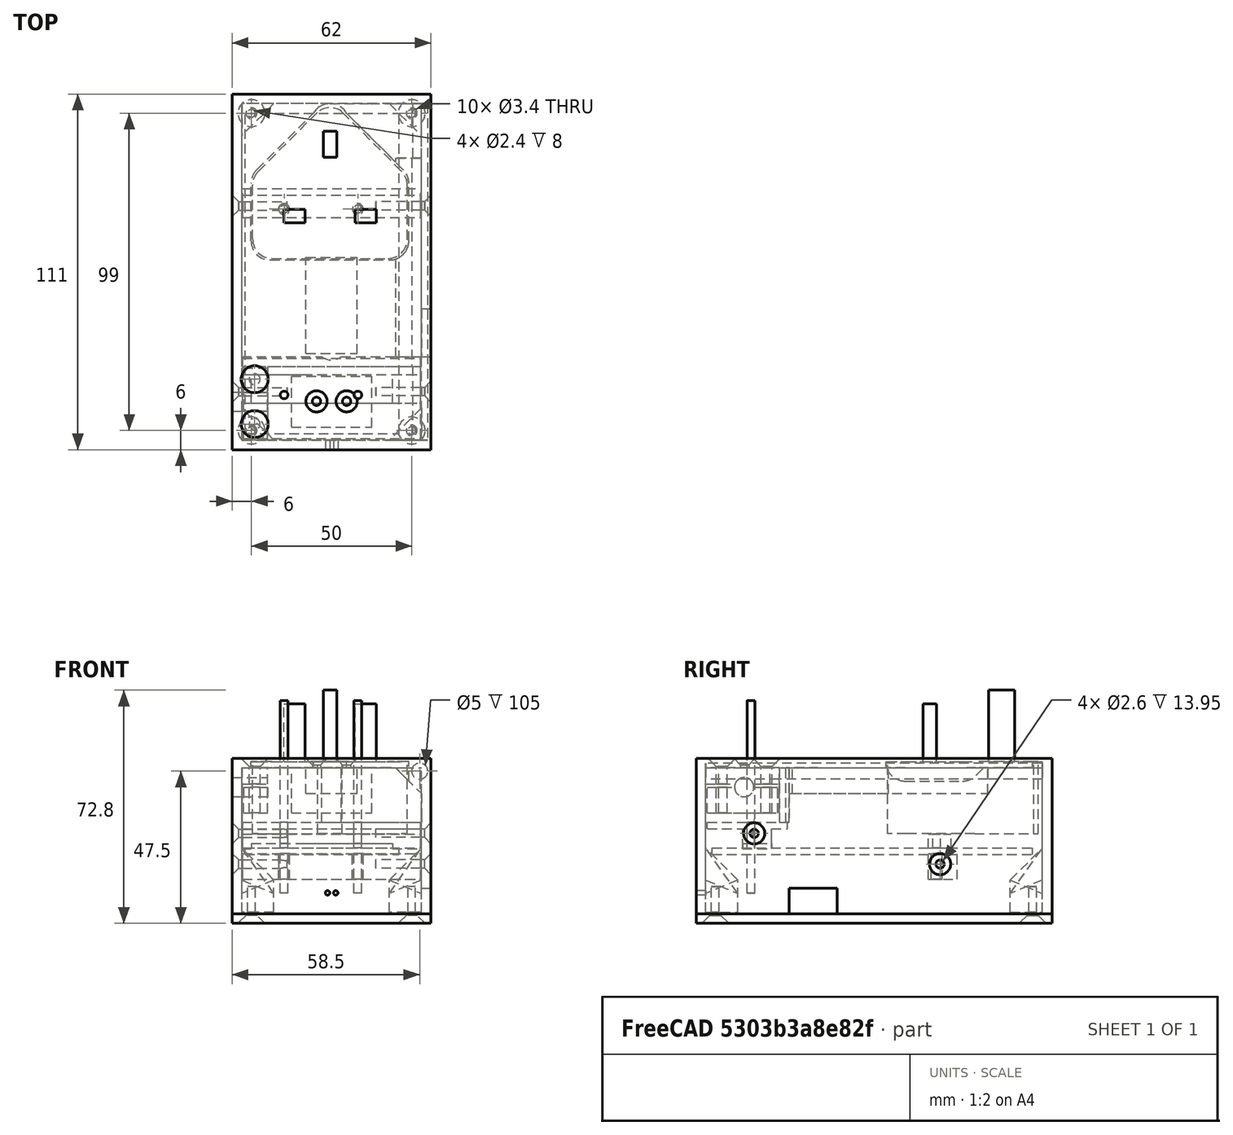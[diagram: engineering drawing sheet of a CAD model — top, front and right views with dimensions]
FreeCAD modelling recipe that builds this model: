
FCSTD DOCUMENT  (FreeCAD 0.16R6703 (Git))
Label: echopi
License: All rights reserved
LicenseURL: http://en.wikipedia.org/wiki/All_rights_reserved
objects: Part::Cut×64, Part::Fuse×35, Part::Box×34, Part::Cylinder×30, Part::Fillet×8, Part::Chamfer×5, Part::Cone×5, Part::Mirroring×5, Part::MultiCommon×2, App::DocumentObjectGroup×1
note: 188 computed .brp shape members not serialized (recipe doc carries the construction recipe); baked Part::Feature solids carry a one-line shape summary decoded from their .brp

FEATURE [Part::Box] Box  label="Cube"
  Height = 18
  Length = 6.6
  Placement = pos=(7.8,-2.2,0) rot=(0,0,1;0rad)
  Width = 4.2
FEATURE [Part::Box] Box001  label="Cube001"
  Height = 18
  Length = 6.6
  Placement = pos=(-14.4,-2.2,0) rot=(0,0,1;0rad)
  Width = 4.2
FEATURE [Part::Box] Box002  label="Cube002"
  Height = 22.3
  Length = 4.2
  Placement = pos=(-2.1,18.2,0) rot=(0,0,1;0rad)
  Width = 8.2
FEATURE [Part::Box] Box003  label="Cube003"
  Height = 50
  Length = 49.2
  Placement = pos=(-24.6,-13.8,-50) rot=(0,0,1;0rad)
  Width = 50.4
FEATURE [Part::Chamfer] Chamfer
  Base = -> Box003
  Edges = 1 edges r=24: [Edge3]
FEATURE [Part::Chamfer] Chamfer001
  Base = -> Chamfer
  Edges = 1 edges r=24: [Edge15]
FEATURE [Part::Fillet] Fillet
  Base = -> Chamfer001
  Edges = 1 edges r=6: [Edge14]
FEATURE [Part::Fillet] Fillet001
  Base = -> Fillet
  Edges = 1 edges r=6: [Edge9]
FEATURE [Part::Fillet] Fillet002
  Base = -> Fillet001
  Edges = 1 edges r=6: [Edge19]
FEATURE [Part::Fillet] Fillet003
  Base = -> Fillet002
  Edges = 1 edges r=6: [Edge17]
FEATURE [Part::Cylinder] Cylinder
  Angle = 360
  Height = 70
  Placement = pos=(0,27.75,-60) rot=(0,0,1;0rad)
  Radius = 6
FEATURE [Part::Box] Box004  label="Cube004"
  Height = 100
  Length = 50
  Placement = pos=(-25,-18,-60) rot=(0,0,1;0rad)
  Width = 50
FEATURE [Part::Fuse] Fusion
  Base = -> Cylinder
  Tool = -> Box004
FEATURE [Part::MultiCommon] Common
  Shapes = -> [Fillet003,Fusion]
FEATURE [Part::Fuse] Fusion001
  Base = -> Box002
  Tool = -> Common
FEATURE [Part::Fuse] Fusion002
  Base = -> Box001
  Tool = -> Fusion001
FEATURE [Part::Fuse] Fusion003  label="plug-blank-a"
  Base = -> Box
  Tool = -> Fusion002
FEATURE [Part::Box] Box005  label="Cube005"
  Height = 48.5
  Length = 62
  Placement = pos=(-31,-73,-48.5) rot=(0,0,1;0rad)
  Width = 111
FEATURE [Part::Box] Box006  label="Cube006"
  Height = 101
  Length = 50
  Placement = pos=(-25,-16,-123.5) rot=(0,0,1;0rad)
  Width = 50
FEATURE [Part::Cut] Cut  label="plug-blank"
  Base = -> Fusion003
  Placement = pos=(-0.5,0,-1) rot=(0,0,1;0rad)
  Tool = -> Box006
FEATURE [Part::Box] Box007  label="Cube007"
  Height = 48
  Length = 56
  Placement = pos=(-28,-70,-51) rot=(0,0,1;0rad)
  Width = 105
FEATURE [Part::Cut] Cut001
  Base = -> Box005
  Tool = -> Box007
FEATURE [Part::Box] Box008  label="pcb"
  Height = 2
  Length = 48
  Placement = pos=(-27,-68,-30) rot=(0,0,1;0rad)
  Width = 100
FEATURE [Part::Cylinder] Cylinder001
  Angle = 360
  Height = 60
  Placement = pos=(-14.8,-55.9,-42) rot=(0,0,1;0rad)
  Radius = 1.2
FEATURE [Part::Cylinder] Cylinder002
  Angle = 360
  Height = 60
  Placement = pos=(8.2,-55.9,-42) rot=(0,0,1;0rad)
  Radius = 1.2
FEATURE [Part::Cylinder] Cylinder003
  Angle = 360
  Height = 60
  Placement = pos=(8.2,2.1,-42) rot=(0,0,1;0rad)
  Radius = 1.2
FEATURE [Part::Cylinder] Cylinder004
  Angle = 360
  Height = 60
  Placement = pos=(-14.8,2.1,-42) rot=(0,0,1;0rad)
  Radius = 1.2
FEATURE [Part::Box] Box009  label="wifi"
  Height = 8
  Length = 30
  Placement = pos=(11,-44,-48.5) rot=(0,0,1;0rad)
  Width = 15
FEATURE [Part::Box] Box010  label="Cube010"
  Height = 8
  Length = 55.5
  Placement = pos=(-27.75,-0.5,-28.5) rot=(0,0,1;0rad)
  Width = 9
FEATURE [Part::Box] Box011  label="Cube011"
  Height = 19
  Length = 42
  Placement = pos=(-9,8.5,-33.5) rot=(0,0,1;0rad)
  Width = 14
FEATURE [Part::Cut] Cut003
  Base = -> Box010
  Placement = pos=(0,0,-9.27) rot=(0,0,1;0rad)
  Tool = -> Box011
FEATURE [Part::Cylinder] Cylinder005
  Angle = 360
  Height = 20
  Placement = pos=(-33.8,3.1,-33) rot=(0,1,0;1.5708rad)
  Radius = 1.3
FEATURE [Part::Cone] Cone
  Angle = 360
  Height = 2
  Placement = pos=(-31,3.1,-33) rot=(0,1,0;1.5708rad)
  Radius1 = 3.3
  Radius2 = 1.3
FEATURE [Part::Fuse] Fusion004  label="countersunk-M2.5"
  Base = -> Cylinder005
  Placement = pos=(-47,13,0) rot=(0,0,1;0rad)
  Tool = -> Cone
FEATURE [Part::Fuse] Fusion005  label="countersunk-M2.006"
  Base = -> Cylinder005
  Tool = -> Cone
FEATURE [Part::Fuse] Fusion006  label="countersunk-M2.007"
  Base = -> Cylinder005
  Tool = -> Cone
FEATURE [Part::Mirroring] Part__Mirroring  label="countersunk-M2.006 (Mirror #1)"
  Base = (0,0,0)
  Normal = (1,0,0)
  Source = -> Fusion005
FEATURE [Part::Fuse] Fusion007  label="countersunk-M2.008"
  Base = -> Cylinder005
  Placement = pos=(0,13,0) rot=(0,0,1;0rad)
  Tool = -> Cone
FEATURE [Part::Mirroring] Part__Mirroring001  label="countersunk-M2.006 (Mirror #1)001"
  Base = (0,0,0)
  Normal = (1,0,0)
  Source = -> Fusion005
FEATURE [Part::Fuse] Fusion008  label="countersunk-M2.009"
  Base = -> Cylinder005
  Tool = -> Cone
FEATURE [Part::Cut] Cut004
  Base = -> Cut001
  Tool = -> Fusion004
FEATURE [Part::Cut] Cut005
  Base = -> Cut004
  Tool = -> Fusion006
FEATURE [Part::Cut] Cut006
  Base = -> Cut005
  Tool = -> Part__Mirroring
FEATURE [Part::Cut] Cut007
  Base = -> Cut003
  Tool = -> Fusion007
FEATURE [Part::Cut] Cut008
  Base = -> Cut007
  Tool = -> Part__Mirroring001
FEATURE [Part::Cut] Cut009
  Base = -> Cut008
  Tool = -> Fusion008
FEATURE [Part::Cut] Cut010
  Base = -> Cut009
  Tool = -> Cylinder003
FEATURE [Part::Cut] Cut011  label="pcb-support-1-b"
  Base = -> Cut010
  Tool = -> Cylinder004
FEATURE [Part::Box] Box012  label="USB-A-plug"
  Height = 8
  Length = 16
  Placement = pos=(-8,-43,-11) rot=(0,0,1;0rad)
  Width = 30
FEATURE [Part::Cut] Cut012
  Base = -> Cut010
  Placement = pos=(0,-58,9.6) rot=(0,0,1;0rad)
  Tool = -> Cylinder004
FEATURE [Part::Fuse] Fusion009  label="countersunk-M2.010"
  Base = -> Cylinder005
  Placement = pos=(-37,-45,9.6) rot=(0,0,1;0rad)
  Tool = -> Cone
FEATURE [Part::Mirroring] Part__Mirroring002  label="countersunk-M2.006 (Mirror #1)002"
  Base = (0,0,0)
  Normal = (1,0,0)
  Placement = pos=(0,-58,9.6) rot=(0,0,1;0rad)
  Source = -> Fusion005
FEATURE [Part::Fuse] Fusion010  label="countersunk-M2.011"
  Base = -> Cylinder005
  Placement = pos=(0,-58,9.6) rot=(0,0,1;0rad)
  Tool = -> Cone
FEATURE [Part::Cut] Cut013
  Base = -> Cut006
  Tool = -> Fusion009
FEATURE [Part::Cut] Cut014
  Base = -> Cut013
  Tool = -> Fusion010
FEATURE [Part::Cut] Cut015
  Base = -> Cut014
  Tool = -> Part__Mirroring002
FEATURE [Part::Box] Box013  label="Cube012"
  Height = 25
  Length = 44
  Placement = pos=(-25,-68,-51.5) rot=(0,0,1;0rad)
  Width = 100
FEATURE [Part::Cut] Cut016  label="pcb-support-2-a"
  Base = -> Cut012
  Tool = -> Box013
FEATURE [Part::Box] Box014  label="screw-con"
  Height = 14
  Length = 25
  Placement = pos=(-12.5,-66,-17) rot=(0,0,1;0rad)
  Width = 16
FEATURE [Part::Fuse] Fusion011  label="countersunk-M2.012"
  Base = -> Cylinder005
  Placement = pos=(37.7,-61,-31) rot=(0,1,0;1.5708rad)
  Tool = -> Cone
FEATURE [Part::Fuse] Fusion012  label="countersunk-M2.013"
  Base = -> Cylinder005
  Placement = pos=(28.3,-61,-31) rot=(0,1,0;1.5708rad)
  Tool = -> Cone
FEATURE [Part::Cut] Cut017
  Base = -> Cut015
  Tool = -> Fusion011
FEATURE [Part::Cut] Cut018
  Base = -> Cut017
  Tool = -> Fusion012
FEATURE [Part::Box] Box015  label="barrier"
  Height = 18
  Length = 58
  Placement = pos=(-29.5,-47,-20) rot=(0,0,1;0rad)
  Width = 3
FEATURE [Part::Box] Box016  label="gallery1"
  Height = 14
  Length = 16
  Placement = pos=(12,18,-17) rot=(0,0,1;0rad)
  Width = 17
FEATURE [Part::Box] Box017  label="gallery2"
  Height = 14
  Length = 16
  Placement = pos=(12,-70,-17) rot=(0,0,1;0rad)
  Width = 23
FEATURE [Part::Cylinder] Cylinder006  label="gallery3"
  Angle = 360
  Height = 105
  Placement = pos=(27.5,35,-4) rot=(1,0,0;1.5708rad)
  Radius = 2.5
FEATURE [Part::Box] Box018  label="Cube013"
  Height = 20
  Length = 10
  Width = 10
FEATURE [Part::Box] Box019  label="Cube014"
  Height = 23
  Length = 21
  Placement = pos=(0,0,-1) rot=(0,0,1;0.785398rad)
  Width = 10
FEATURE [Part::Cut] Cut022
  Base = -> Box018
  Tool = -> Box019
FEATURE [Part::Box] Box020  label="Cube015"
  Height = 10
  Length = 29
  Placement = pos=(-9.86396,-4.94975,7.13604) rot=(-0.678598,-0.678598,-0.281085;1.09606rad)
  Width = 24
FEATURE [Part::Cut] Cut023
  Base = -> Cut022
  Placement = pos=(18,-70,-48) rot=(0,0,1;0rad)
  Tool = -> Box020
FEATURE [Part::Cut] Cut024
  Base = -> Cut022
  Placement = pos=(28,25,-48) rot=(0,0,1;1.5708rad)
  Tool = -> Box020
FEATURE [Part::Cut] Cut025
  Base = -> Cut022
  Placement = pos=(-18,35,-48) rot=(0,0,1;3.14159rad)
  Tool = -> Box020
FEATURE [Part::Box] Box021  label="screw-con001"
  Height = 6
  Length = 8
  Placement = pos=(-28,-70,-8) rot=(0,0,1;0rad)
  Width = 23
FEATURE [Part::Cylinder] Cylinder007  label="cable"
  Angle = 360
  Height = 20
  Placement = pos=(-34,-58,-9) rot=(0.57735,0.57735,0.57735;2.0944rad)
  Radius = 3
FEATURE [Part::Cylinder] Cylinder008  label="Cylinder006"
  Angle = 360
  Height = 50
  Placement = pos=(-24,-65,-19) rot=(0,0,1;0rad)
  Radius = 1.7
FEATURE [Part::Cylinder] Cylinder009  label="Cylinder007"
  Angle = 360
  Height = 50
  Placement = pos=(-24,-51,-18) rot=(0,0,1;0rad)
  Radius = 1.7
FEATURE [Part::Box] Box022  label="screw-con002"
  Height = 8
  Length = 7.5
  Placement = pos=(-27.5,-69.5,-17) rot=(0,0,1;0rad)
  Width = 22
FEATURE [Part::Cone] Cone001
  Angle = 360
  Height = 2.5
  Placement = pos=(-24,-51,-2.5) rot=(0,0,1;0rad)
  Radius1 = 1.7
  Radius2 = 4.2
FEATURE [Part::Cone] Cone002
  Angle = 360
  Height = 2.5
  Placement = pos=(-24,-65,-2.5) rot=(0,0,1;0rad)
  Radius1 = 1.7
  Radius2 = 4.2
FEATURE [Part::Cylinder] Cylinder010  label="Cylinder021"
  Angle = 360
  Height = 50
  Placement = pos=(-24,-65,-19) rot=(0,0,1;0rad)
  Radius = 1.7
FEATURE [Part::Cylinder] Cylinder011  label="Cylinder027"
  Angle = 360
  Height = 50
  Placement = pos=(-24,-51,-18) rot=(0,0,1;0rad)
  Radius = 1.7
FEATURE [Part::Cut] Cut031
  Base = -> Box022
  Tool = -> Cylinder010
FEATURE [Part::Cut] Cut032
  Base = -> Cut031
  Tool = -> Cylinder011
FEATURE [Part::Cylinder] Cylinder012  label="cable001"
  Angle = 360
  Height = 20
  Placement = pos=(-34,-58,-9) rot=(0.57735,0.57735,0.57735;2.0944rad)
  Radius = 3
FEATURE [Part::Cut] Cut034  label="cable-clamp"
  Base = -> Cut032
  Tool = -> Cylinder007
FEATURE [Part::Box] Box023  label="lid-a"
  Height = 3
  Length = 62
  Placement = pos=(-31,-73,-51.5) rot=(0,0,1;0rad)
  Width = 111
FEATURE [Part::Cone] Cone003
  Angle = 360
  Height = 2.5
  Placement = pos=(-25,-67,-51.5) rot=(0,0,1;0rad)
  Radius1 = 4.2
  Radius2 = 1.7
FEATURE [Part::Cylinder] Cylinder013  label="Cylinder028"
  Angle = 360
  Height = 50
  Placement = pos=(-25,-67,-90) rot=(0,0,1;0rad)
  Radius = 1.2
FEATURE [Part::Cylinder] Cylinder014  label="Cylinder029"
  Angle = 360
  Height = 50
  Placement = pos=(-25,-67,-90) rot=(0,0,1;0rad)
  Radius = 1.7
FEATURE [Part::Fuse] Fusion019
  Base = -> Cone003
  Tool = -> Cylinder014
FEATURE [Part::Cylinder] Cylinder015  label="Cylinder030"
  Angle = 360
  Height = 50
  Placement = pos=(25,-67,-90) rot=(0,0,1;0rad)
  Radius = 1.2
FEATURE [Part::Cylinder] Cylinder016  label="Cylinder031"
  Angle = 360
  Height = 50
  Placement = pos=(-25,32,-90) rot=(0,0,1;0rad)
  Radius = 1.2
FEATURE [Part::Cylinder] Cylinder017  label="Cylinder032"
  Angle = 360
  Height = 50
  Placement = pos=(25,32,-90) rot=(0,0,1;0rad)
  Radius = 1.2
FEATURE [Part::Fuse] Fusion021
  Base = -> Cone003
  Placement = pos=(50,0,0) rot=(0,0,1;0rad)
  Tool = -> Cylinder014
FEATURE [Part::Fuse] Fusion022
  Base = -> Cone003
  Placement = pos=(0,99,0) rot=(0,0,1;0rad)
  Tool = -> Cylinder014
FEATURE [Part::Fuse] Fusion023
  Base = -> Cone003
  Placement = pos=(50,99,0) rot=(0,0,1;0rad)
  Tool = -> Cylinder014
FEATURE [Part::Cut] Cut039
  Base = -> Box023
  Tool = -> Fusion021
FEATURE [Part::Cut] Cut040
  Base = -> Cut039
  Tool = -> Fusion019
FEATURE [Part::Cut] Cut041
  Base = -> Cut040
  Tool = -> Fusion023
FEATURE [Part::Cut] Cut042  label="lid"
  Base = -> Cut041
  Tool = -> Fusion022
FEATURE [Part::Cylinder] Cylinder018  label="Cylinder033"
  Angle = 360
  Height = 21
  Placement = pos=(0,-40,-24) rot=(0,0,1;0rad)
  Radius = 5
FEATURE [Part::Box] Box024  label="Cube016"
  Height = 18
  Length = 6.6
  Placement = pos=(7.8,-2.2,0) rot=(0,0,1;0rad)
  Width = 4.2
FEATURE [Part::Box] Box025  label="Cube017"
  Height = 18
  Length = 6.6
  Placement = pos=(-14.4,-2.2,0) rot=(0,0,1;0rad)
  Width = 4.2
FEATURE [Part::Box] Box026  label="Cube018"
  Height = 22.3
  Length = 4.2
  Placement = pos=(-2.1,18.2,0) rot=(0,0,1;0rad)
  Width = 8.2
FEATURE [Part::Box] Box027  label="Cube019"
  Height = 50
  Length = 48.2
  Placement = pos=(-24.1,-13.3,-50) rot=(0,0,1;0rad)
  Width = 49.4
FEATURE [Part::Chamfer] Chamfer003
  Base = -> Box027
  Edges = 1 edges r=24: [Edge3]
FEATURE [Part::Chamfer] Chamfer004
  Base = -> Chamfer003
  Edges = 1 edges r=24: [Edge15]
FEATURE [Part::Fillet] Fillet004
  Base = -> Chamfer004
  Edges = 1 edges r=6: [Edge14]
FEATURE [Part::Fillet] Fillet005
  Base = -> Fillet004
  Edges = 1 edges r=6: [Edge9]
FEATURE [Part::Fillet] Fillet006
  Base = -> Fillet005
  Edges = 1 edges r=6: [Edge19]
FEATURE [Part::Fillet] Fillet007
  Base = -> Fillet006
  Edges = 1 edges r=6: [Edge17]
FEATURE [Part::Cylinder] Cylinder019  label="Cylinder034"
  Angle = 360
  Height = 70
  Placement = pos=(0,27.75,-60) rot=(0,0,1;0rad)
  Radius = 6
FEATURE [Part::Box] Box028  label="Cube020"
  Height = 100
  Length = 50
  Placement = pos=(-25,-18,-60) rot=(0,0,1;0rad)
  Width = 50
FEATURE [Part::Fuse] Fusion024
  Base = -> Cylinder019
  Tool = -> Box028
FEATURE [Part::MultiCommon] Common001
  Shapes = -> [Fillet007,Fusion024]
FEATURE [Part::Fuse] Fusion025
  Base = -> Box026
  Tool = -> Common001
FEATURE [Part::Fuse] Fusion026
  Base = -> Box025
  Tool = -> Fusion025
FEATURE [Part::Fuse] Fusion027  label="plug-blank-a001"
  Base = -> Box024
  Tool = -> Fusion026
FEATURE [Part::Box] Box029  label="Cube021"
  Height = 101
  Length = 50
  Placement = pos=(-25,-16,-123.5) rot=(0,0,1;0rad)
  Width = 50
FEATURE [Part::Cut] Cut046  label="13A-charger"
  Base = -> Fusion027
  Placement = pos=(-0.5,0,-1) rot=(0,0,1;0rad)
  Tool = -> Box029
FEATURE [Part::Box] Box030  label="Cube022"
  Height = 2
  Length = 55.5
  Placement = pos=(-27.75,-69.5,-22) rot=(0,0,1;0rad)
  Width = 25
FEATURE [Part::Fuse] Fusion028  label="pcb-support-2-f"
  Base = -> Cut016
  Tool = -> Box030
FEATURE [Part::Box] Box031  label="Cube023"
  Height = 48.5
  Length = 62
  Placement = pos=(-31,-73,-48.5) rot=(0,0,1;0rad)
  Width = 111
FEATURE [Part::Box] Box032  label="Cube024"
  Height = 48
  Length = 56
  Placement = pos=(-28,-70,-51) rot=(0,0,1;0rad)
  Width = 105
FEATURE [Part::Cut] Cut047
  Base = -> Box031
  Tool = -> Box032
FEATURE [Part::Cylinder] Cylinder020  label="Cylinder035"
  Angle = 360
  Height = 20
  Placement = pos=(-33.8,3.1,-33) rot=(0,1,0;1.5708rad)
  Radius = 1.3
FEATURE [Part::Cone] Cone004
  Angle = 360
  Height = 2
  Placement = pos=(-31,3.1,-33) rot=(0,1,0;1.5708rad)
  Radius1 = 3.3
  Radius2 = 1.3
FEATURE [Part::Fuse] Fusion029  label="countersunk-M2.014"
  Base = -> Cylinder020
  Placement = pos=(-47,13,0) rot=(0,0,1;0rad)
  Tool = -> Cone004
FEATURE [Part::Fuse] Fusion030  label="countersunk-M2.015"
  Base = -> Cylinder020
  Tool = -> Cone004
FEATURE [Part::Fuse] Fusion031  label="countersunk-M2.016"
  Base = -> Cylinder020
  Tool = -> Cone004
FEATURE [Part::Mirroring] Part__Mirroring003  label="countersunk-M2.006 (Mirror #1)003"
  Base = (0,0,0)
  Normal = (1,0,0)
  Source = -> Fusion030
FEATURE [Part::Cut] Cut048
  Base = -> Cut047
  Tool = -> Fusion029
FEATURE [Part::Cut] Cut049
  Base = -> Cut048
  Tool = -> Fusion031
FEATURE [Part::Cut] Cut050
  Base = -> Cut049
  Tool = -> Part__Mirroring003
FEATURE [Part::Fuse] Fusion032  label="countersunk-M2.017"
  Base = -> Cylinder020
  Placement = pos=(-37,-45,9.6) rot=(0,0,1;0rad)
  Tool = -> Cone004
FEATURE [Part::Mirroring] Part__Mirroring004  label="countersunk-M2.006 (Mirror #1)004"
  Base = (0,0,0)
  Normal = (1,0,0)
  Placement = pos=(0,-58,9.6) rot=(0,0,1;0rad)
  Source = -> Fusion030
FEATURE [Part::Fuse] Fusion033  label="countersunk-M2.018"
  Base = -> Cylinder020
  Placement = pos=(0,-58,9.6) rot=(0,0,1;0rad)
  Tool = -> Cone004
FEATURE [Part::Cut] Cut051
  Base = -> Cut050
  Tool = -> Fusion032
FEATURE [Part::Cut] Cut052
  Base = -> Cut051
  Tool = -> Fusion033
FEATURE [Part::Cut] Cut053
  Base = -> Cut052
  Tool = -> Part__Mirroring004
FEATURE [Part::Fuse] Fusion034  label="countersunk-M2.019"
  Base = -> Cylinder020
  Placement = pos=(37.7,-61,-31) rot=(0,1,0;1.5708rad)
  Tool = -> Cone004
FEATURE [Part::Fuse] Fusion035  label="countersunk-M2.020"
  Base = -> Cylinder020
  Placement = pos=(28.3,-61,-31) rot=(0,1,0;1.5708rad)
  Tool = -> Cone004
FEATURE [Part::Cut] Cut054
  Base = -> Cut053
  Tool = -> Fusion034
FEATURE [Part::Cut] Cut055
  Base = -> Cut054
  Tool = -> Fusion035
FEATURE [App::DocumentObjectGroup] Group  label="construction"
  Group = -> [Cylinder001,Cylinder002,Cut055]
FEATURE [Part::Cut] Cut026
  Base = -> Cut022
  Placement = pos=(-28,-60,-48) rot=(0,0,-1;1.5708rad)
  Tool = -> Box020
FEATURE [Part::Chamfer] Chamfer005
  Base = -> Cut018
  Edges = 1 edges r=8: [Edge32]
FEATURE [Part::Fuse] Fusion036
  Base = -> Box015
  Tool = -> Chamfer005
FEATURE [Part::Cut] Cut056
  Base = -> Fusion036
  Tool = -> Box017
FEATURE [Part::Cut] Cut057
  Base = -> Cut056
  Tool = -> Box016
FEATURE [Part::Cut] Cut058
  Base = -> Cut057
  Tool = -> Cylinder006
FEATURE [Part::Fuse] Fusion037
  Base = -> Box021
  Tool = -> Cut058
FEATURE [Part::Cut] Cut059
  Base = -> Fusion037
  Tool = -> Cylinder008
FEATURE [Part::Cut] Cut060
  Base = -> Cut059
  Tool = -> Cylinder009
FEATURE [Part::Cut] Cut061
  Base = -> Cut060
  Tool = -> Cylinder012
FEATURE [Part::Cut] Cut062
  Base = -> Cut061
  Tool = -> Cone001
FEATURE [Part::Cut] Cut063
  Base = -> Cut062
  Tool = -> Cone002
FEATURE [Part::Fuse] Fusion038
  Base = -> Cut024
  Tool = -> Cut063
FEATURE [Part::Fuse] Fusion039
  Base = -> Cut025
  Tool = -> Fusion038
FEATURE [Part::Fuse] Fusion040
  Base = -> Cut026
  Tool = -> Fusion039
FEATURE [Part::Fuse] Fusion041
  Base = -> Cut023
  Tool = -> Fusion040
FEATURE [Part::Cut] Cut064
  Base = -> Fusion041
  Tool = -> Cylinder013
FEATURE [Part::Cut] Cut065
  Base = -> Cut064
  Tool = -> Cylinder015
FEATURE [Part::Cut] Cut066
  Base = -> Cut065
  Tool = -> Cylinder016
FEATURE [Part::Cut] Cut067
  Base = -> Cut066
  Tool = -> Cylinder017
FEATURE [Part::Cut] Cut068
  Base = -> Cut067
  Tool = -> Box009
FEATURE [Part::Cut] Cut069
  Base = -> Cut068
  Tool = -> Cylinder018
FEATURE [Part::Cut] Cut070  label="body-d"
  Base = -> Cut069
  Tool = -> Cut
FEATURE [Part::Cylinder] Cylinder022  label="Cylinder036"
  Angle = 360
  Height = 10
  Placement = pos=(1.27,-67,-42) rot=(1,0,0;1.5708rad)
  Radius = 0.7
FEATURE [Part::Cylinder] Cylinder023  label="Cylinder037"
  Angle = 360
  Height = 10
  Placement = pos=(-1.27,-67,-42) rot=(1,0,0;1.5708rad)
  Radius = 0.7
FEATURE [Part::Cut] Cut071
  Base = -> Cut070
  Tool = -> Cylinder022
FEATURE [Part::Cut] Cut072  label="body-d001"
  Base = -> Cut071
  Tool = -> Cylinder023
FEATURE [Part::Cylinder] Cylinder024  label="Cylinder038"
  Angle = 360
  Height = 60
  Placement = pos=(-14.8,-55.9,-42) rot=(0,0,1;0rad)
  Radius = 1.2
FEATURE [Part::Cylinder] Cylinder025  label="Cylinder039"
  Angle = 360
  Height = 60
  Placement = pos=(8.2,-55.9,-42) rot=(0,0,1;0rad)
  Radius = 1.2
FEATURE [Part::Cut] Cut073
  Base = -> Fusion028
  Tool = -> Cylinder024
FEATURE [Part::Cut] Cut074  label="pcb-support-2"
  Base = -> Cut073
  Tool = -> Cylinder025
FEATURE [Part::Cylinder] Cylinder026  label="Cylinder040"
  Angle = 360
  Height = 70
  Placement = pos=(-0.5,29,-71) rot=(0,0,1;0rad)
  Radius = 6
FEATURE [Part::Cut] Cut075  label="body"
  Base = -> Cut072
  Tool = -> Cylinder026
FEATURE [Part::Box] Box033  label="Cube025"
  Height = 4.4
  Length = 55.5
  Placement = pos=(-27.75,-0.5,-28) rot=(0,0,1;0rad)
  Width = 7
FEATURE [Part::Cylinder] Cylinder027  label="Cylinder043"
  Angle = 360
  Height = 60
  Placement = pos=(8.2,2.1,-42) rot=(0,0,1;0rad)
  Radius = 1.2
FEATURE [Part::Cylinder] Cylinder028  label="Cylinder044"
  Angle = 360
  Height = 60
  Placement = pos=(-14.8,2.1,-42) rot=(0,0,1;0rad)
  Radius = 1.2
FEATURE [Part::Cut] Cut076
  Base = -> Box033
  Tool = -> Cylinder027
FEATURE [Part::Cut] Cut077  label="spacer"
  Base = -> Cut076
  Tool = -> Cylinder028
FEATURE [Part::Cylinder] Cylinder029  label="Cylinder047"
  Angle = 360
  Height = 60
  Placement = pos=(8.2,2.1,-42) rot=(0,0,1;0rad)
  Radius = 1.7
FEATURE [Part::Cylinder] Cylinder030  label="Cylinder048"
  Angle = 360
  Height = 60
  Placement = pos=(-14.8,2.1,-42) rot=(0,0,1;0rad)
  Radius = 1.7
FEATURE [Part::Cut] Cut078
  Base = -> Cut011
  Tool = -> Cylinder029
FEATURE [Part::Cut] Cut079  label="pcb-support-1"
  Base = -> Cut078
  Tool = -> Cylinder030
